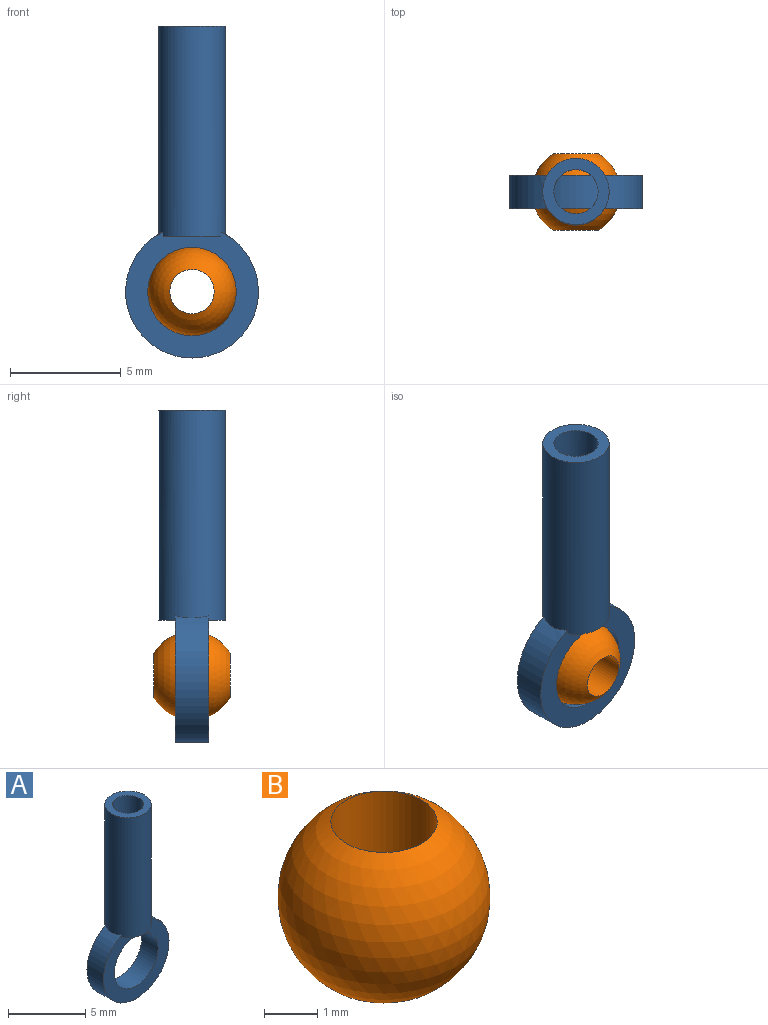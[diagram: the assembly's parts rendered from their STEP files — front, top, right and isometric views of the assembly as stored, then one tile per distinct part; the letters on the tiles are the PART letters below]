
ASSEMBLY  parts=2 mates=1
PART A: 10 faces, bbox 6x3x15 mm
  f0: cylinder r=3mm len=6mm, axis (0,1,0), area 23.8mm2, adj f3,f4,f7
  f1: cylinder r=2mm len=4mm, axis (0,1,0), area 18.8mm2, adj f3,f4
  f2: cylinder r=3mm len=2mm, axis (0,1,0), area 2.7mm2, adj f3,f4,f6
  f3: plane 6x6mm, normal (0,-1,0), area 15.3mm2, adj f0,f1,f2,f6,f7,f9
  f4: plane 6x6mm, normal (0,1,0), area 15.3mm2, adj f0,f1,f2,f5,f6,f7
  f5: plane 2.6x0.75mm, normal (0,0,-1), area 1.2mm2, adj f4,f6,f7
  f6: cylinder r=1mm len=9.5mm, axis (0,0,-1), area 58.5mm2, adj f2,f3,f4,f5,f8,f9
  f7: cylinder r=1.5mm len=9.5mm, axis (0,0,-1), area 89.1mm2, adj f0,f3,f4,f5,f8,f9
  f8: plane 3x3mm, normal (0,0,1), area 3.9mm2, adj f6,f7
  f9: plane 2.6x0.75mm, normal (0,0,-1), area 1.2mm2, adj f3,f6,f7
PART B: 2 faces, bbox 4x4x3.5 mm
  f0: sphere r=2mm, area 43.5mm2, adj f1
  f1: cylinder r=1mm len=3.46mm, axis (0,0,1), area 21.8mm2, adj f0
PLACE A at identity fixed
PLACE B rot(axis=(-1,0,0),90deg) t=(21.07,0,0)mm
MATE ball A.f0 <-> B.f1  axis (0,1,0) through (21.07,0,0)mm
